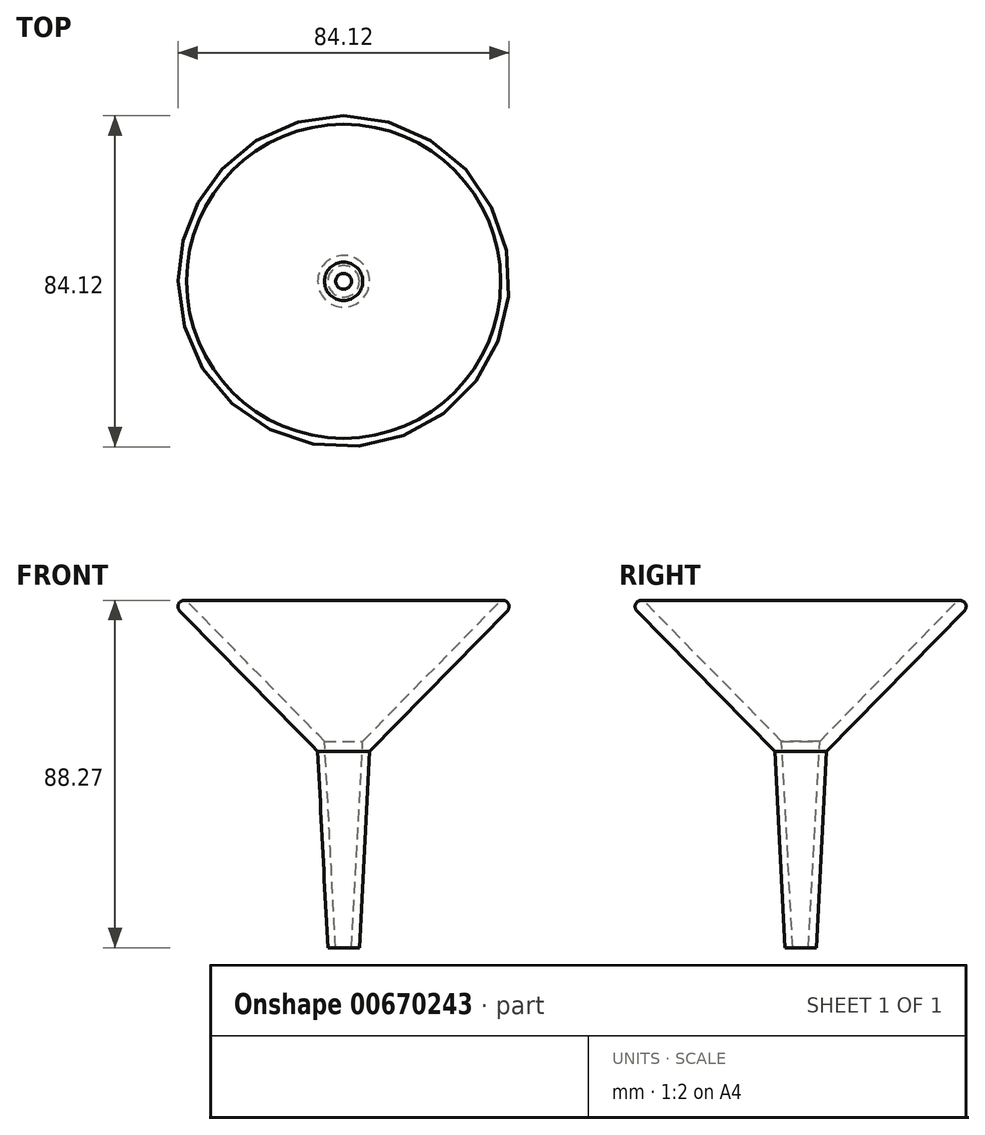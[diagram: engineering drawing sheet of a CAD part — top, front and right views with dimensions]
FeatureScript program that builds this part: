
annotation { "Feature Type Name" : "Feature", "Feature Type Description" : "" }
export const myFeature = defineFeature(function(context is Context, id is Id, definition is map)
    precondition{}
    {
        {
            var Q0;
            Q0=qCreatedBy(makeId("Front.planeOp"),FACE);
            var sketch = newSketch(context, id + "F0", { "sketchPlane" : qUnion([Q0])});
            skLineSegment(sketch, "E0", {"start": v(4.86, 52.47) * mm, "end": v(39.9, 88.15) * mm});
            skLineSegment(sketch, "E1", {"start": v(6.58, 49.93) * mm, "end": v(41.6, 85.6) * mm});
            skArc(sketch, "E2", {"start": v(41.6, 85.6) * mm, "mid": v(41.79, 87.58) * mm, "end": v(39.9, 88.15) * mm});
            skLineSegment(sketch, "E3", {"start": v(4.86, 52.47) * mm, "end": v(2, 0) * mm});
            skLineSegment(sketch, "E4", {"start": v(6.58, 49.93) * mm, "end": v(4, 0) * mm});
            skLineSegment(sketch, "E5", {"start": v(2, 0) * mm, "end": v(4, 0) * mm});
            skLineSegment(sketch, "E6", {"start": v(0, 0) * mm, "end": v(0, 20.74) * mm});
            skSolve(sketch);
        }
        {
            var Q0;
            Q0 = qSketchRegion(id + "F0", true);
            var Q1;
            Q1=sQuery(id+"F0.wireOp",EDGE,"E6");
            revolve(context, id + "F1", {"entities" : qUnion([Q0]), "axis" : qUnion([Q1]), "revolveType" : RevolveType.FULL});
        }
    });
